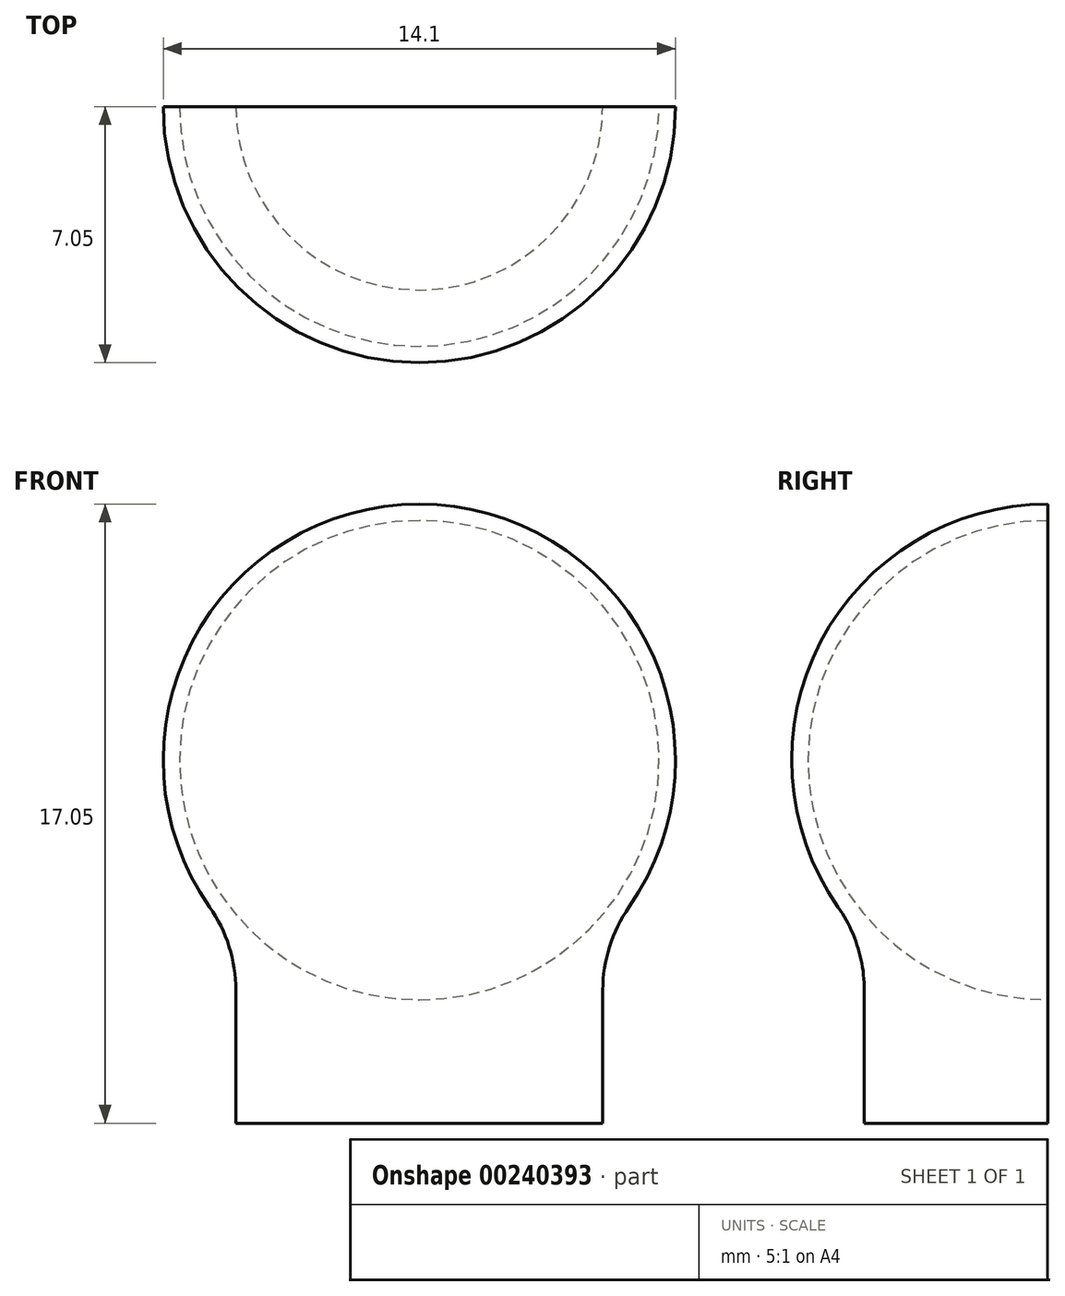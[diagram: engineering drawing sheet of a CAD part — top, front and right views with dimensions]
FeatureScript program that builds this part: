
annotation { "Feature Type Name" : "Feature", "Feature Type Description" : "" }
export const myFeature = defineFeature(function(context is Context, id is Id, definition is map)
    precondition{}
    {
        {
            var Q0;
            Q0=qCreatedBy(makeId("Front.planeOp"),FACE);
            var sketch = newSketch(context, id + "F0", { "sketchPlane" : qUnion([Q0])});
            skCircle(sketch, "E0", {"center": v(0, 10) * mm, "radius": 6.6 * mm});
            skCircle(sketch, "E1", {"center": v(0, 10) * mm, "radius": 7.05 * mm});
            skLineSegment(sketch, "E2", {"start": v(0, 17.05) * mm, "end": v(0, 2.95) * mm});
            skLineSegment(sketch, "E3.bottom", {"start": v(5.05, 0) * mm, "end": v(-5.05, 0) * mm});
            skLineSegment(sketch, "E3.top", {"start": v(5.05, 5.9) * mm, "end": v(-5.05, 5.9) * mm});
            skLineSegment(sketch, "E3.left", {"start": v(5.05, 0) * mm, "end": v(5.05, 5.9) * mm});
            skLineSegment(sketch, "E3.right", {"start": v(-5.05, 0) * mm, "end": v(-5.05, 5.9) * mm});
            skPoint(sketch, "E3.middle", {"position": v(0, 2.95) * mm});
            skLineSegment(sketch, "E4", {"start": v(0, 2.95) * mm, "end": v(0, 0) * mm});
            skSolve(sketch);
        }
        {
            var Q0;
            {var subQ0=sQuery(id+"F0.wireOp",EDGE,"E2");var subQ1=sQuery(id+"F0.wireOp",EDGE,"E0");var subQ2=makeQuery(id+"F0.imprint","INTERSECT",VERTEX,{"disambiguationData":[OD(0.0)],"derivedFrom":[subQ1,subQ0]});Q0=makeQuery(id+"F0.imprint","IMPRINT",FACE,{"disambiguationData":[TD([[makeQuery(id+"F0.imprint","IMPRINT",EDGE,{"disambiguationData":[TD([[subQ2,1.0]])],"derivedFrom":subQ1}),-1.0]])]});}
            var Q1;
            {var subQ0=sQuery(id+"F0.wireOp",EDGE,"E2");var subQ1=sQuery(id+"F0.wireOp",EDGE,"E0");var subQ2=makeQuery(id+"F0.imprint","INTERSECT",VERTEX,{"disambiguationData":[OD(1.0)],"derivedFrom":[subQ1,subQ0]});Q1=makeQuery(id+"F0.imprint","IMPRINT",FACE,{"disambiguationData":[TD([[makeQuery(id+"F0.imprint","IMPRINT",EDGE,{"disambiguationData":[TD([[subQ2,-1.0]])],"derivedFrom":subQ1}),-1.0]])]});}
            var Q2;
            {var subQ0=sQuery(id+"F0.wireOp",EDGE,"E4");Q2=makeQuery(id+"F0.imprint","IMPRINT",FACE,{"disambiguationData":[TD([[makeQuery(id+"F0.imprint","IMPRINT",EDGE,{"derivedFrom":subQ0}),1.0]])]});}
            var Q3;
            Q3=sQuery(id+"F0.wireOp",EDGE,"E2");
            revolve(context, id + "F1", {"entities" : qUnion([Q0, Q1, Q2]), "axis" : qUnion([Q3]), "revolveType" : RevolveType.ONE_DIRECTION, "angle" : 180 * degree});
        }
        {
            var Q0;
            Q0=makeQuery(id+"F1.opRevolve","SWEPT_EDGE",EDGE,{"disambiguationData":[OSD([sQuery(id+"F0.wireOp",EDGE,"E1"),sQuery(id+"F0.wireOp",EDGE,"E3.left")])]});
            fillet(context, id + "F2", {"entities" : qUnion([Q0]), "radius" : 4 * mm, "tangentPropagation" : true, "allowEdgeOverflow" : false});
        }
    });
